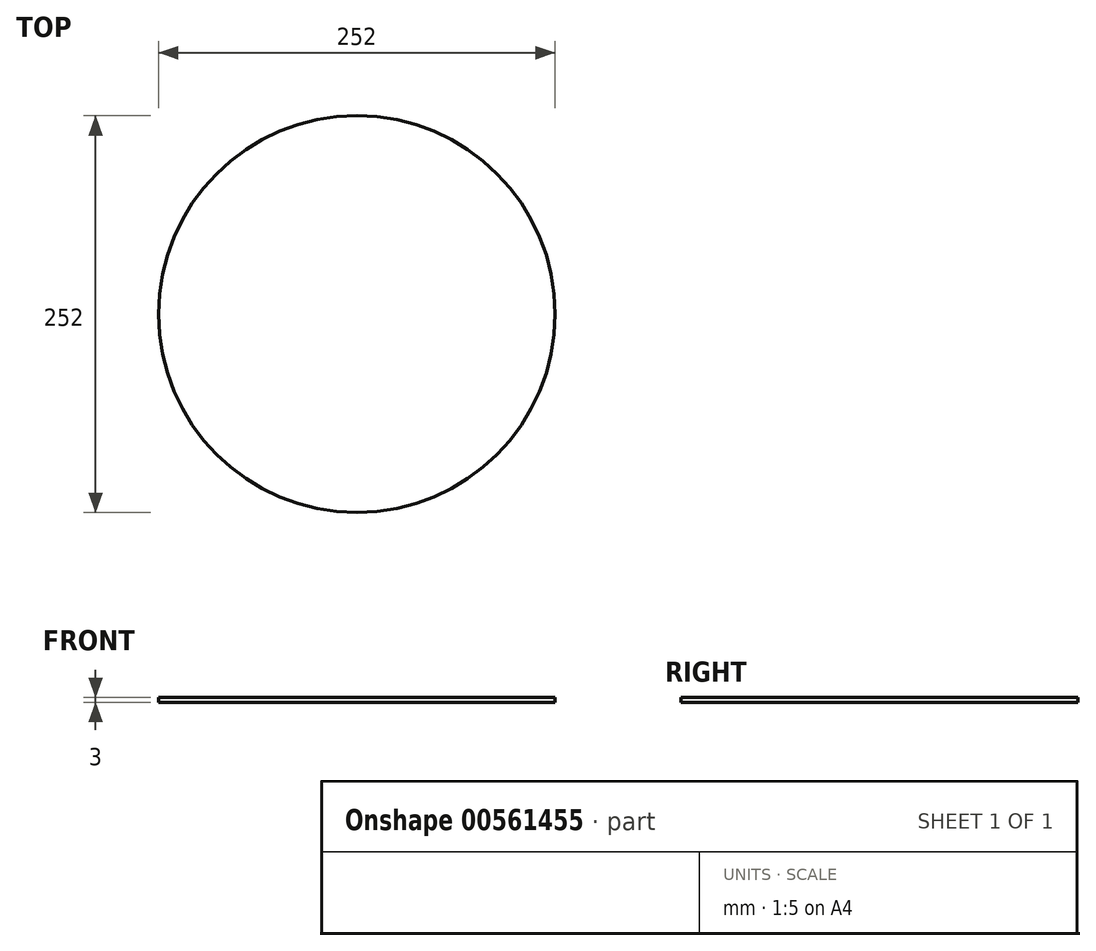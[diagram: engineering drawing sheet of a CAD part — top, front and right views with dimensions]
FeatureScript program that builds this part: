
annotation { "Feature Type Name" : "Feature", "Feature Type Description" : "" }
export const myFeature = defineFeature(function(context is Context, id is Id, definition is map)
    precondition{}
    {
        {
            var Q0;
            Q0=qCreatedBy(makeId("Top.planeOp"),FACE);
            var sketch = newSketch(context, id + "F0", { "sketchPlane" : qUnion([Q0])});
            skCircle(sketch, "E0", {"center": v(0, 0) * mm, "radius": 126 * mm});
            skSolve(sketch);
        }
        {
            var Q0;
            Q0=makeQuery(id+"F0.imprint","IMPRINT",FACE,{"disambiguationData":[TD([[makeQuery(id+"F0.imprint","IMPRINT",EDGE,{"derivedFrom":sQuery(id+"F0.wireOp",EDGE,"E0")}),1.0]])]});
            extrude(context, id + "F1", {"entities" : qUnion([Q0]), "depth" : 3 * mm, "offsetDistance" : 25 * mm});
        }
    });
